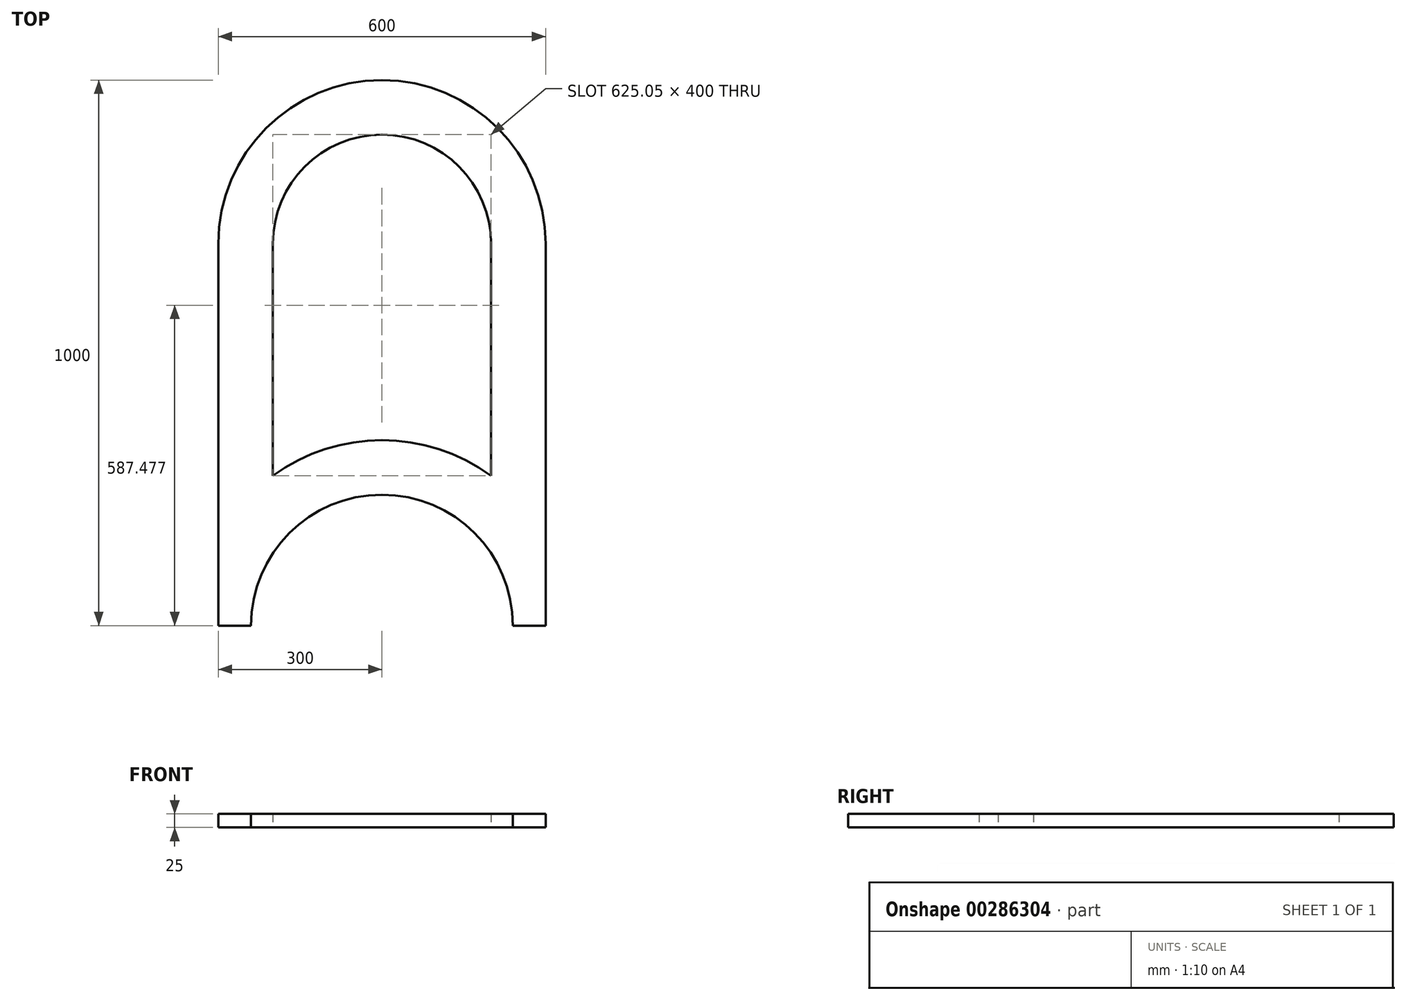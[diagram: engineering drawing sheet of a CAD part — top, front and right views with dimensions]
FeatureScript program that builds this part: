
annotation { "Feature Type Name" : "Feature", "Feature Type Description" : "" }
export const myFeature = defineFeature(function(context is Context, id is Id, definition is map)
    precondition{}
    {
        {
            var Q0;
            Q0=qCreatedBy(makeId("Top.planeOp"),FACE);
            var sketch = newSketch(context, id + "F0", { "sketchPlane" : qUnion([Q0])});
            skLineSegment(sketch, "E0", {"start": v(0, -300) * mm, "end": v(0, -1000) * mm});
            skLineSegment(sketch, "E1", {"start": v(0, -1000) * mm, "end": v(60, -1000) * mm});
            skLineSegment(sketch, "E2", {"start": v(300, 0) * mm, "end": v(300, 0) * mm});
            skLineSegment(sketch, "E3", {"start": v(600, -300) * mm, "end": v(600, -1000) * mm});
            skLineSegment(sketch, "E4", {"start": v(600, -1000) * mm, "end": v(540, -1000) * mm});
            skArc(sketch, "E5", {"start": v(540, -1000) * mm, "mid": v(300, -760) * mm, "end": v(60, -1000) * mm});
            skPoint(sketch, "E6.visualSharp", {"position": v(0, 0) * mm});
            skArc(sketch, "E6.filletArc", {"start": v(300, 0) * mm, "mid": v(87.87, -87.87) * mm, "end": v(0, -300) * mm});
            skPoint(sketch, "E7.visualSharp", {"position": v(600, 0) * mm});
            skArc(sketch, "E7.filletArc", {"start": v(600, -300) * mm, "mid": v(512.13, -87.87) * mm, "end": v(300, 0) * mm});
            skArc(sketch, "E8", {"start": v(500, -725.05) * mm, "mid": v(300, -660) * mm, "end": v(100, -725.05) * mm});
            skLineSegment(sketch, "E9", {"start": v(300, 0) * mm, "end": v(300, -100) * mm});
            skArc(sketch, "E10", {"start": v(500, -300) * mm, "mid": v(300, -100) * mm, "end": v(100, -300) * mm});
            skLineSegment(sketch, "E11", {"start": v(100, -300) * mm, "end": v(100, -725.05) * mm});
            skLineSegment(sketch, "E12", {"start": v(500, -300) * mm, "end": v(500, -725.05) * mm});
            skSolve(sketch);
        }
        {
            var Q0;
            Q0=makeQuery(id+"F0.imprint","IMPRINT",FACE,{"disambiguationData":[TD([[makeQuery(id+"F0.imprint","IMPRINT",EDGE,{"derivedFrom":sQuery(id+"F0.wireOp",EDGE,"E0")}),1.0]])]});
            extrude(context, id + "F1", {"entities" : qUnion([Q0]), "depth" : 25 * mm});
        }
    });
